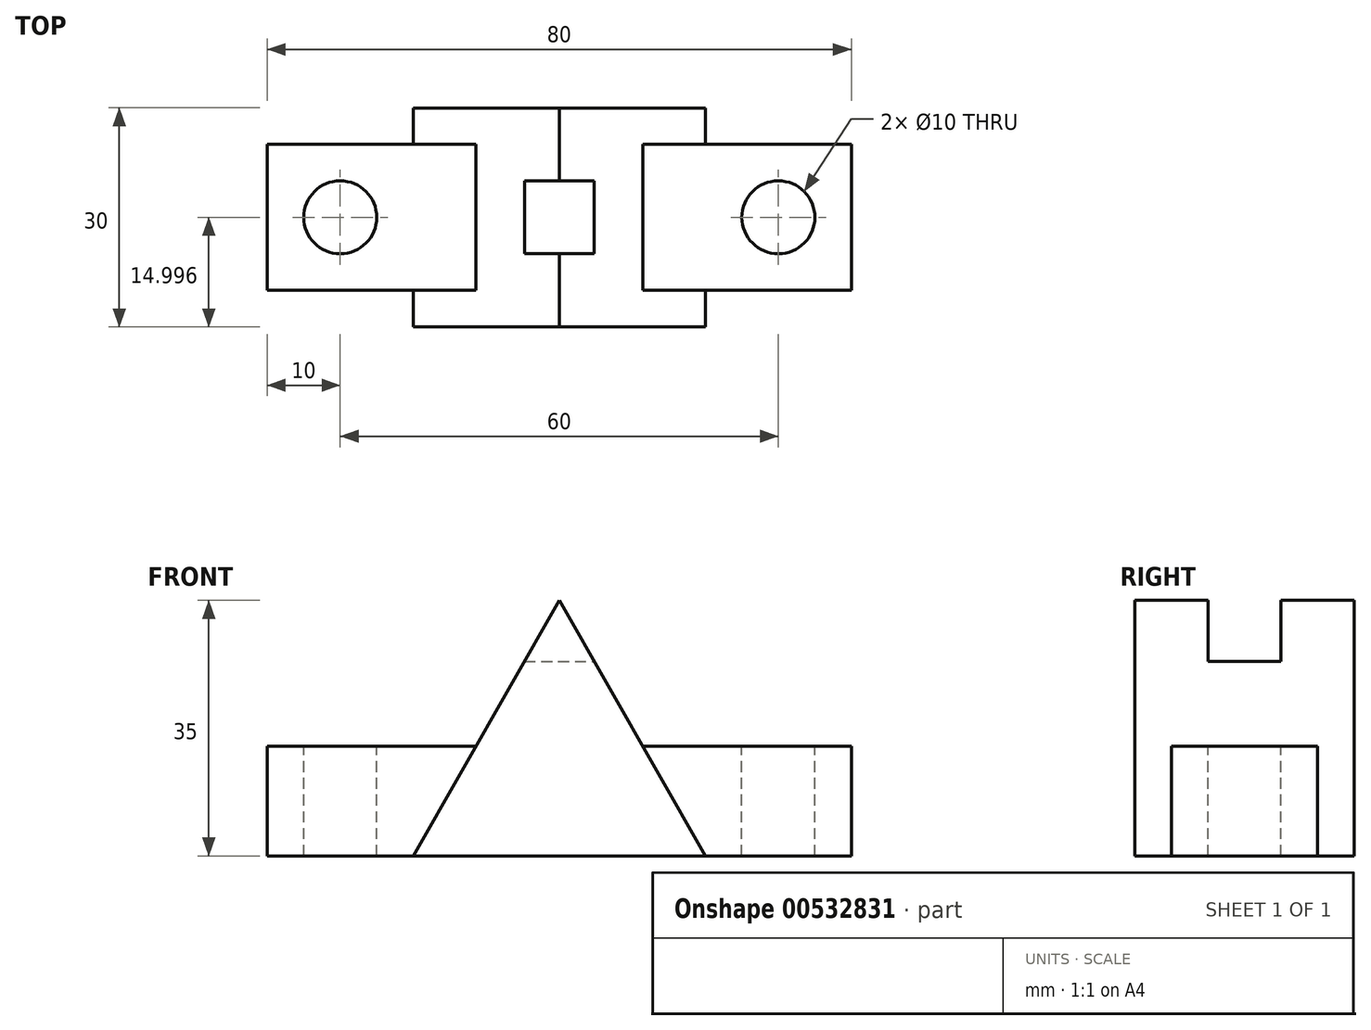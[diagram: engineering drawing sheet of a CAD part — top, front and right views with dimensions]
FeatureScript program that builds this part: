
annotation { "Feature Type Name" : "Feature", "Feature Type Description" : "" }
export const myFeature = defineFeature(function(context is Context, id is Id, definition is map)
    precondition{}
    {
        {
            var Q0;
            Q0=qCreatedBy(makeId("Right.planeOp"),FACE);
            var sketch = newSketch(context, id + "F0", { "sketchPlane" : qUnion([Q0])});
            skLineSegment(sketch, "E0.bottom", {"start": v(-43.51, -11.67) * mm, "end": v(-23.51, -11.67) * mm});
            skLineSegment(sketch, "E0.top", {"start": v(-43.51, -26.67) * mm, "end": v(-23.51, -26.67) * mm});
            skLineSegment(sketch, "E0.left", {"start": v(-43.51, -11.67) * mm, "end": v(-43.51, -26.67) * mm});
            skLineSegment(sketch, "E0.right", {"start": v(-23.51, -11.67) * mm, "end": v(-23.51, -26.67) * mm});
            skSolve(sketch);
        }
        {
            var Q0;
            Q0 = qSketchRegion(id + "F0", true);
            extrude(context, id + "F1", {"entities" : qUnion([Q0]), "depth" : 80 * mm, "offsetDistance" : 25.4 * mm});
        }
        {
            var Q0;
            Q0=makeQuery(id+"F1.opExtrude","SWEPT_FACE",FACE,{"disambiguationData":[OSD([sQuery(id+"F0.wireOp",EDGE,"E0.left")])]});
            var sketch = newSketch(context, id + "F2", { "sketchPlane" : qUnion([Q0])});
            skLineSegment(sketch, "E1", {"start": v(40, -26.67) * mm, "end": v(40, 8.33) * mm});
            skPoint(sketch, "E1.endSnap0", {"position": v(40, -11.67) * mm});
            skLineSegment(sketch, "E2", {"start": v(40, -26.67) * mm, "end": v(20, -26.67) * mm});
            skLineSegment(sketch, "E3", {"start": v(40, -26.67) * mm, "end": v(60, -26.67) * mm});
            skLineSegment(sketch, "E4", {"start": v(40, 8.33) * mm, "end": v(20, -26.67) * mm});
            skLineSegment(sketch, "E5", {"start": v(60, -26.67) * mm, "end": v(40, 8.33) * mm});
            skSolve(sketch);
        }
        {
            var Q0;
            Q0 = qSketchRegion(id + "F2", true);
            extrude(context, id + "F3", {"entities" : qUnion([Q0]), "operationType" : NewBodyOperationType.ADD, "oppositeDirection" : true, "depth" : 25 * mm, "offsetDistance" : 25.4 * mm, "hasSecondDirection" : true, "secondDirectionOppositeDirection" : false, "secondDirectionDepth" : 5 * mm});
        }
        {
            var Q0;
            Q0=qCreatedBy(makeId("Top.planeOp"),FACE);
            var sketch = newSketch(context, id + "F4", { "sketchPlane" : qUnion([Q0])});
            skLineSegment(sketch, "E6.bottom", {"start": v(33.65, -28.51) * mm, "end": v(46.35, -28.51) * mm});
            skLineSegment(sketch, "E6.top", {"start": v(33.65, -38.51) * mm, "end": v(46.35, -38.51) * mm});
            skLineSegment(sketch, "E6.left", {"start": v(33.65, -28.51) * mm, "end": v(33.65, -38.51) * mm});
            skLineSegment(sketch, "E6.right", {"start": v(46.35, -28.51) * mm, "end": v(46.35, -38.51) * mm});
            skSolve(sketch);
        }
        {
            var Q0;
            Q0 = qSketchRegion(id + "F4", true);
            extrude(context, id + "F5", {"entities" : qUnion([Q0]), "operationType" : NewBodyOperationType.REMOVE, "depth" : 8.38 * mm, "offsetDistance" : 25.4 * mm});
        }
        {
            var Q0;
            {var subQ2=sQuery(id+"F0.wireOp",EDGE,"E0.bottom");Q0=makeQuery(id+"F3.boolean.opBoolean","SPLIT",FACE,{"disambiguationData":[TD([makeQuery(id+"F3.opExtrude","SWEPT_FACE",FACE,{"disambiguationData":[OSD([sQuery(id+"F2.wireOp",EDGE,"E4")])]})])],"derivedFrom":makeQuery(id+"F1.opExtrude","SWEPT_FACE",FACE,{"disambiguationData":[OSD([subQ2])]})});}
            var sketch = newSketch(context, id + "F6", { "sketchPlane" : qUnion([Q0])});
            skCircle(sketch, "E7", {"center": v(10, -33.51) * mm, "radius": 5 * mm});
            skCircle(sketch, "E8", {"center": v(70, -33.51) * mm, "radius": 5 * mm});
            skSolve(sketch);
        }
        {
            var Q0;
            Q0 = qSketchRegion(id + "F6", true);
            extrude(context, id + "F7", {"entities" : qUnion([Q0]), "operationType" : NewBodyOperationType.REMOVE, "oppositeDirection" : true, "depth" : 25.4 * mm, "offsetDistance" : 25.4 * mm});
        }
    });
